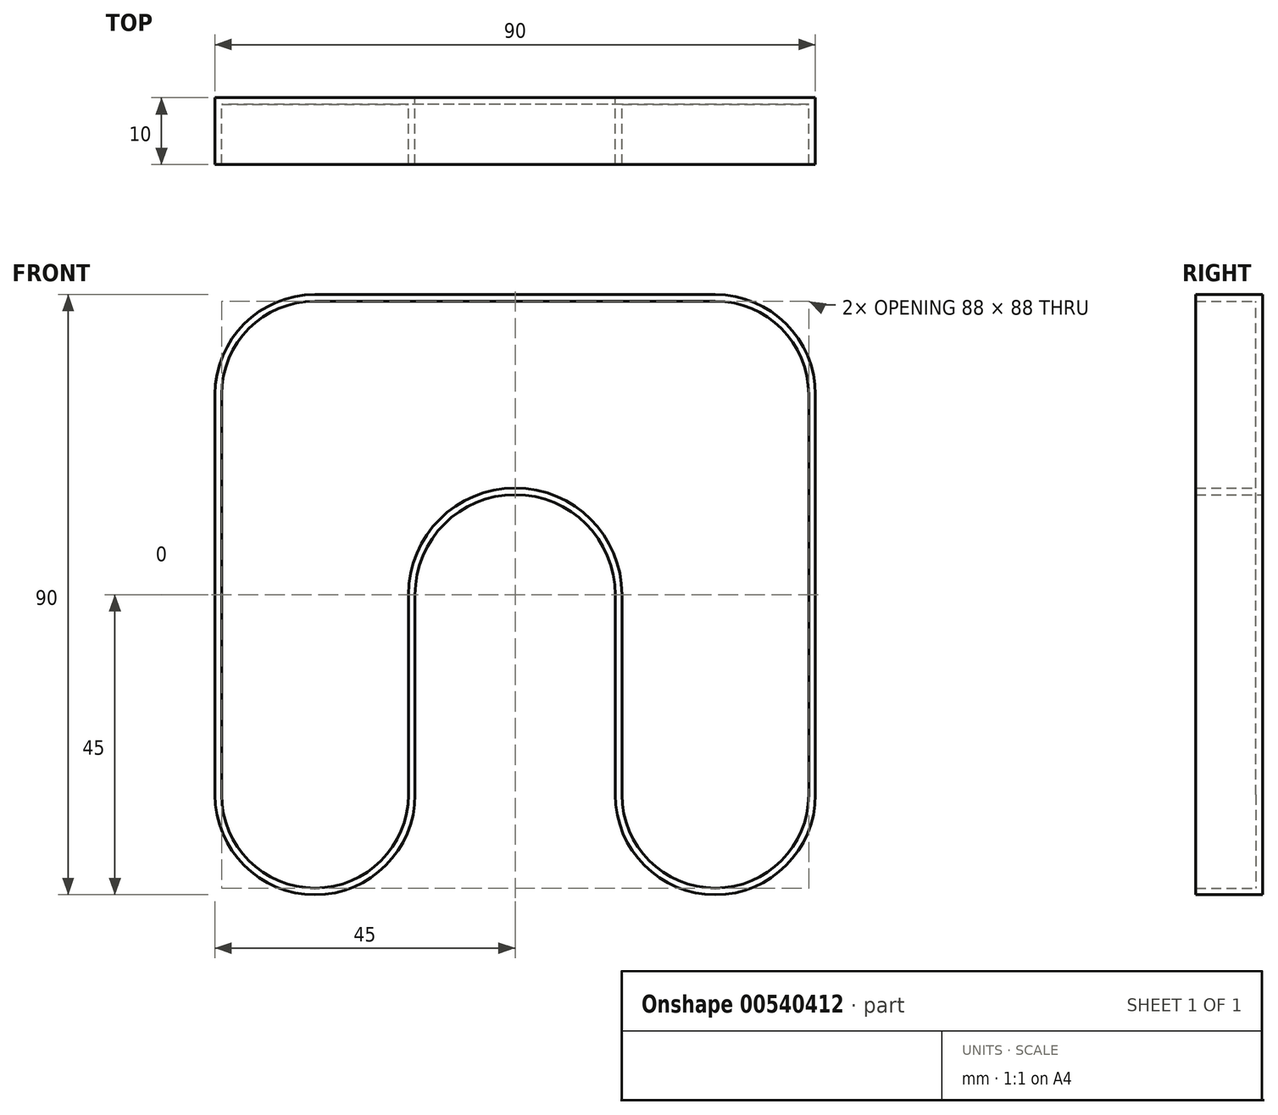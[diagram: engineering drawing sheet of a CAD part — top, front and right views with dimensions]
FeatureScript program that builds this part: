
annotation { "Feature Type Name" : "Feature", "Feature Type Description" : "" }
export const myFeature = defineFeature(function(context is Context, id is Id, definition is map)
    precondition{}
    {
        {
            var Q0;
            Q0=qCreatedBy(makeId("Front.planeOp"),FACE);
            var sketch = newSketch(context, id + "F0", { "sketchPlane" : qUnion([Q0])});
            skLineSegment(sketch, "E0.top", {"start": v(30, 45) * mm, "end": v(-30, 45) * mm});
            skLineSegment(sketch, "E0.left", {"start": v(45, -30) * mm, "end": v(45, 30) * mm});
            skLineSegment(sketch, "E0.right", {"start": v(-45, -30) * mm, "end": v(-45, 30) * mm});
            skPoint(sketch, "E0.middle", {"position": v(0, 0) * mm});
            skLineSegment(sketch, "E1", {"start": v(-30, -45) * mm, "end": v(-30, -45) * mm});
            skLineSegment(sketch, "E2", {"start": v(-15, -30) * mm, "end": v(-15, 0) * mm});
            skLineSegment(sketch, "E3", {"start": v(0, 15) * mm, "end": v(0, 15) * mm});
            skLineSegment(sketch, "E4", {"start": v(15, 0) * mm, "end": v(15, -30) * mm});
            skLineSegment(sketch, "E5", {"start": v(30, -45) * mm, "end": v(30, -45) * mm});
            skPoint(sketch, "E6.visualSharp", {"position": v(45, 45) * mm});
            skArc(sketch, "E6.filletArc", {"start": v(45, 30) * mm, "mid": v(40.6, 40.6) * mm, "end": v(30, 45) * mm});
            skPoint(sketch, "E7.visualSharp", {"position": v(-45, 45) * mm});
            skArc(sketch, "E7.filletArc", {"start": v(-30, 45) * mm, "mid": v(-40.6, 40.6) * mm, "end": v(-45, 30) * mm});
            skPoint(sketch, "E8.visualSharp", {"position": v(-45, -45) * mm});
            skArc(sketch, "E8.filletArc", {"start": v(-45, -30) * mm, "mid": v(-40.6, -40.6) * mm, "end": v(-30, -45) * mm});
            skPoint(sketch, "E9.visualSharp", {"position": v(-15, -45) * mm});
            skArc(sketch, "E9.filletArc", {"start": v(-30, -45) * mm, "mid": v(-19.4, -40.6) * mm, "end": v(-15, -30) * mm});
            skPoint(sketch, "E10.visualSharp", {"position": v(15, -45) * mm});
            skArc(sketch, "E10.filletArc", {"start": v(15, -30) * mm, "mid": v(19.4, -40.6) * mm, "end": v(30, -45) * mm});
            skPoint(sketch, "E11.visualSharp", {"position": v(45, -45) * mm});
            skArc(sketch, "E11.filletArc", {"start": v(30, -45) * mm, "mid": v(40.6, -40.6) * mm, "end": v(45, -30) * mm});
            skPoint(sketch, "E12.visualSharp", {"position": v(15, 15) * mm});
            skArc(sketch, "E12.filletArc", {"start": v(15, 0) * mm, "mid": v(10.6, 10.6) * mm, "end": v(0, 15) * mm});
            skPoint(sketch, "E13.visualSharp", {"position": v(-15, 15) * mm});
            skArc(sketch, "E13.filletArc", {"start": v(0, 15) * mm, "mid": v(-10.6, 10.6) * mm, "end": v(-15, 0) * mm});
            skSolve(sketch);
        }
        {
            var Q0;
            Q0=makeQuery(id+"F0.imprint","IMPRINT",FACE,{"disambiguationData":[TD([[makeQuery(id+"F0.imprint","IMPRINT",EDGE,{"derivedFrom":sQuery(id+"F0.wireOp",EDGE,"E0.top")}),1.0]])]});
            extrude(context, id + "F1", {"entities" : qUnion([Q0]), "depth" : 10 * mm, "offsetDistance" : 25 * mm});
        }
        {
            var Q0;
            Q0=makeQuery(id+"F1.opExtrude","CAP_FACE",FACE,{"disambiguationData":[OSD([sQuery(id+"F0.wireOp",EDGE,"E0.top"),sQuery(id+"F0.wireOp",EDGE,"E0.left"),sQuery(id+"F0.wireOp",EDGE,"E0.right"),sQuery(id+"F0.wireOp",EDGE,"E2"),sQuery(id+"F0.wireOp",EDGE,"E4"),sQuery(id+"F0.wireOp",EDGE,"E6.filletArc"),sQuery(id+"F0.wireOp",EDGE,"E7.filletArc"),sQuery(id+"F0.wireOp",EDGE,"E8.filletArc"),sQuery(id+"F0.wireOp",EDGE,"E9.filletArc"),sQuery(id+"F0.wireOp",EDGE,"E10.filletArc"),sQuery(id+"F0.wireOp",EDGE,"E11.filletArc"),sQuery(id+"F0.wireOp",EDGE,"E12.filletArc"),sQuery(id+"F0.wireOp",EDGE,"E13.filletArc")])],"isStart":false});
            shell(context, id + "F2", {"entities" : qUnion([Q0]), "thickness" : 1 * mm});
        }
    });
